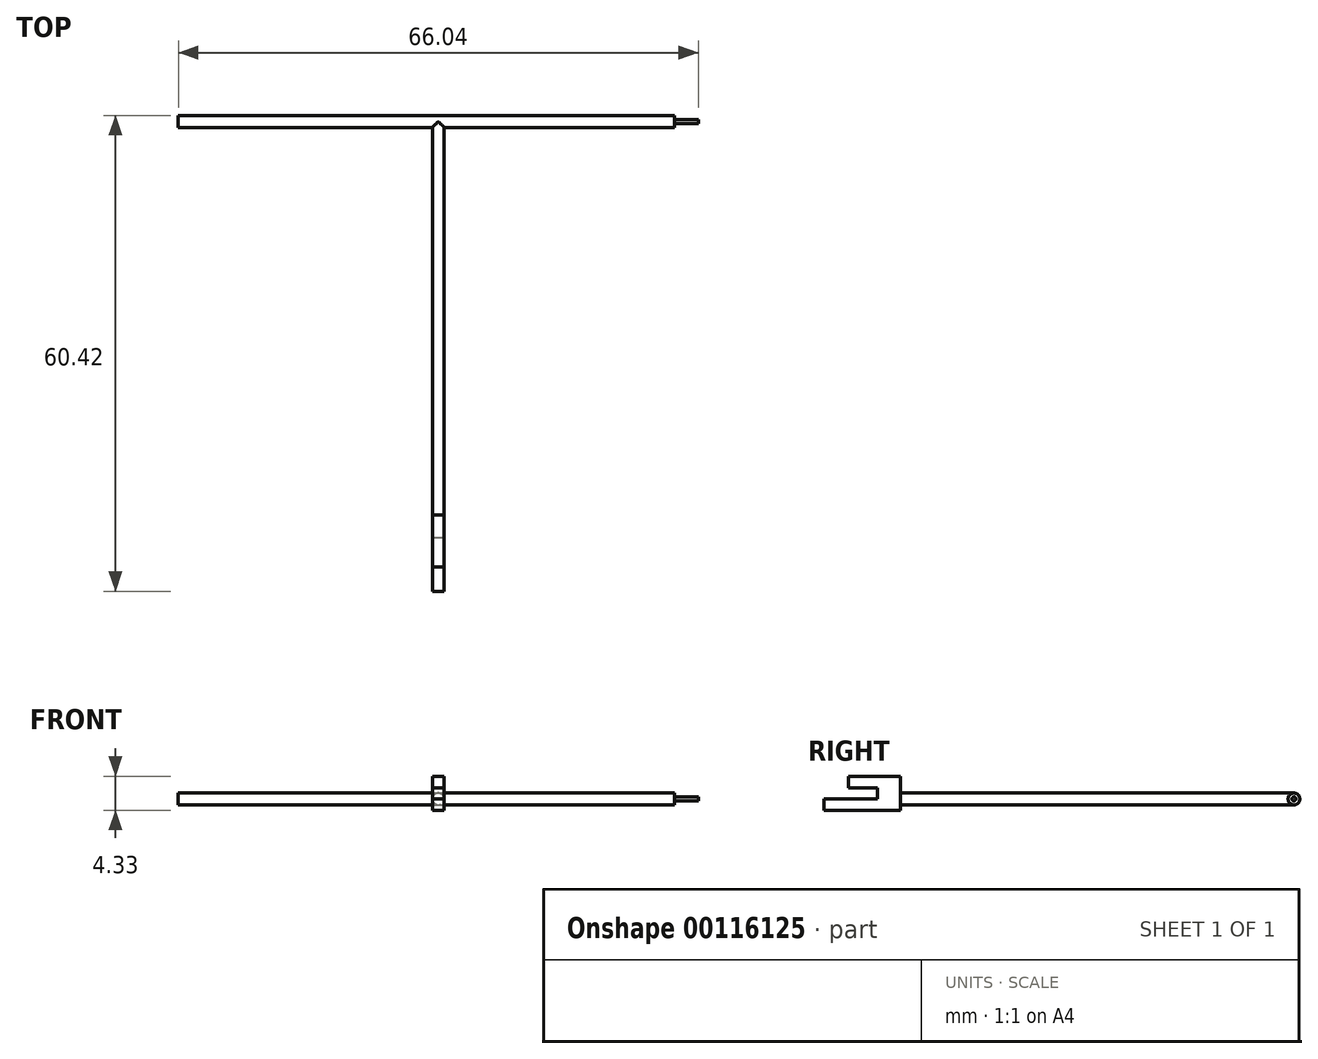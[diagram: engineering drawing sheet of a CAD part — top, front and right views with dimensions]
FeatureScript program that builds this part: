
annotation { "Feature Type Name" : "Feature", "Feature Type Description" : "" }
export const myFeature = defineFeature(function(context is Context, id is Id, definition is map)
    precondition{}
    {
        {
            var Q0;
            Q0=qCreatedBy(makeId("Front.planeOp"),FACE);
            var sketch = newSketch(context, id + "F0", { "sketchPlane" : qUnion([Q0])});
            skLineSegment(sketch, "E0", {"start": v(0, 0) * mm, "end": v(-30, 0) * mm});
            skLineSegment(sketch, "E1", {"start": v(0, 0) * mm, "end": v(30, 0) * mm});
            skLineSegment(sketch, "E2", {"start": v(30, 0) * mm, "end": v(35, 0) * mm});
            skLineSegment(sketch, "E3", {"start": v(-30, 0) * mm, "end": v(-35, 0) * mm});
            skSolve(sketch);
        }
        {
            var Q0;
            Q0=sQuery(id+"F0.wireOp",VERTEX,"E3.start");
            var Q1;
            Q1=qCreatedBy(makeId("Right.planeOp"),FACE);
            cPlane(context, id + "F1", {"entities" : qUnion([Q0, Q1]), "cplaneType" : CPlaneType.PLANE_POINT, "offset" : 25.4 * mm, "width" : 152.4 * mm, "height" : 152.4 * mm});
        }
        {
            var Q0;
            Q0=qCreatedBy(id+"F1.planeOp",FACE);
            var sketch = newSketch(context, id + "F2", { "sketchPlane" : qUnion([Q0])});
            skCircle(sketch, "E4", {"center": v(0, 0) * mm, "radius": 0.75 * mm});
            skSolve(sketch);
        }
        {
            var Q0;
            Q0=makeQuery(id+"F2.imprint","IMPRINT",FACE,{"disambiguationData":[TD([[makeQuery(id+"F2.imprint","IMPRINT",EDGE,{"derivedFrom":sQuery(id+"F2.wireOp",EDGE,"E4")}),1.0]])]});
            var Q1;
            Q1=sQuery(id+"F0.wireOp",EDGE,"E0");
            var Q2;
            Q2=sQuery(id+"F0.wireOp",EDGE,"E1");
            sweep(context, id + "F3", {"profiles" : qUnion([Q0]), "path" : qUnion([Q1, Q2])});
        }
        {
            var Q0;
            Q0=qCreatedBy(makeId("Front.planeOp"),FACE);
            var sketch = newSketch(context, id + "F4", { "sketchPlane" : qUnion([Q0])});
            skLineSegment(sketch, "E5", {"start": v(0, 0) * mm, "end": v(-33.02, 0) * mm});
            skSolve(sketch);
        }
        {
            var Q0;
            Q0=sQuery(id+"F4.wireOp",VERTEX,"E5.end");
            var Q1;
            Q1=qCreatedBy(makeId("Right.planeOp"),FACE);
            cPlane(context, id + "F5", {"entities" : qUnion([Q0, Q1]), "cplaneType" : CPlaneType.PLANE_POINT, "offset" : 25.4 * mm, "width" : 152.4 * mm, "height" : 152.4 * mm});
        }
        {
            var Q0;
            Q0=qCreatedBy(id+"F5.planeOp",FACE);
            var sketch = newSketch(context, id + "F6", { "sketchPlane" : qUnion([Q0])});
            skCircle(sketch, "E6", {"center": v(0, 0) * mm, "radius": 0.25 * mm});
            skSolve(sketch);
        }
        {
            var Q0;
            Q0=makeQuery(id+"F6.imprint","IMPRINT",FACE,{"disambiguationData":[TD([[makeQuery(id+"F6.imprint","IMPRINT",EDGE,{"derivedFrom":sQuery(id+"F6.wireOp",EDGE,"E6")}),1.0]])]});
            var Q1;
            Q1 = qSketchRegion(id + "F2", true);
            var Q2;
            Q2=sQuery(id+"F4.wireOp",EDGE,"E5");
            sweep(context, id + "F7", {"operationType" : NewBodyOperationType.ADD, "profiles" : qUnion([Q0, Q1]), "path" : qUnion([Q2])});
        }
        {
            var Q0;
            Q0=qCreatedBy(makeId("Front.planeOp"),FACE);
            var sketch = newSketch(context, id + "F8", { "sketchPlane" : qUnion([Q0])});
            skLineSegment(sketch, "E7", {"start": v(0, 0) * mm, "end": v(33.02, 0) * mm});
            skSolve(sketch);
        }
        {
            var Q0;
            Q0=sQuery(id+"F8.wireOp",VERTEX,"E7.end");
            var Q1;
            Q1=qCreatedBy(makeId("Right.planeOp"),FACE);
            cPlane(context, id + "F9", {"entities" : qUnion([Q0, Q1]), "cplaneType" : CPlaneType.PLANE_POINT, "offset" : 25.4 * mm, "width" : 152.4 * mm, "height" : 152.4 * mm});
        }
        {
            var Q0;
            Q0=qCreatedBy(id+"F9.planeOp",FACE);
            var sketch = newSketch(context, id + "F10", { "sketchPlane" : qUnion([Q0])});
            skCircle(sketch, "E8", {"center": v(0, 0) * mm, "radius": 0.25 * mm});
            skSolve(sketch);
        }
        {
            var Q0;
            Q0=makeQuery(id+"F10.imprint","IMPRINT",FACE,{"disambiguationData":[TD([[makeQuery(id+"F10.imprint","IMPRINT",EDGE,{"derivedFrom":sQuery(id+"F10.wireOp",EDGE,"E8")}),1.0]])]});
            var Q1;
            Q1=sQuery(id+"F8.wireOp",EDGE,"E7");
            sweep(context, id + "F11", {"operationType" : NewBodyOperationType.ADD, "profiles" : qUnion([Q0]), "path" : qUnion([Q1])});
        }
        {
            var Q0;
            Q0=qCreatedBy(makeId("Origin.pointOp"),VERTEX);
            var Q1;
            Q1=qCreatedBy(makeId("Right.planeOp"),FACE);
            cPlane(context, id + "F12", {"entities" : qUnion([Q0, Q1]), "cplaneType" : CPlaneType.PLANE_POINT, "offset" : 25.4 * mm, "width" : 152.4 * mm, "height" : 152.4 * mm});
        }
        {
            var Q0;
            Q0=qCreatedBy(id+"F12.planeOp",FACE);
            var sketch = newSketch(context, id + "F13", { "sketchPlane" : qUnion([Q0])});
            skLineSegment(sketch, "E9", {"start": v(0, 0) * mm, "end": v(-50, 0) * mm});
            skSolve(sketch);
        }
        {
            var Q0;
            Q0=sQuery(id+"F13.wireOp",VERTEX,"E9.end");
            var Q1;
            Q1=qCreatedBy(makeId("Front.planeOp"),FACE);
            cPlane(context, id + "F14", {"entities" : qUnion([Q0, Q1]), "cplaneType" : CPlaneType.PLANE_POINT, "offset" : 25.4 * mm, "width" : 152.4 * mm, "height" : 152.4 * mm});
        }
        {
            var Q0;
            Q0=qCreatedBy(id+"F14.planeOp",FACE);
            var sketch = newSketch(context, id + "F15", { "sketchPlane" : qUnion([Q0])});
            skCircle(sketch, "E10", {"center": v(0, 0) * mm, "radius": 0.75 * mm});
            skSolve(sketch);
        }
        {
            var Q0;
            Q0=makeQuery(id+"F15.imprint","IMPRINT",FACE,{"disambiguationData":[TD([[makeQuery(id+"F15.imprint","IMPRINT",EDGE,{"derivedFrom":sQuery(id+"F15.wireOp",EDGE,"E10")}),1.0]])]});
            var Q1;
            Q1=sQuery(id+"F13.wireOp",EDGE,"E9");
            sweep(context, id + "F16", {"operationType" : NewBodyOperationType.ADD, "profiles" : qUnion([Q0]), "path" : qUnion([Q1])});
        }
        {
            var Q0;
            Q0=sQuery(id+"F13.wireOp",VERTEX,"E9.end");
            var Q1;
            Q1=qCreatedBy(makeId("Right.planeOp"),FACE);
            cPlane(context, id + "F17", {"entities" : qUnion([Q0, Q1]), "cplaneType" : CPlaneType.PLANE_POINT, "offset" : 25.4 * mm, "width" : 152.4 * mm, "height" : 152.4 * mm});
        }
        {
            var Q0;
            Q0=qCreatedBy(id+"F17.planeOp",FACE);
            var sketch = newSketch(context, id + "F18", { "sketchPlane" : qUnion([Q0])});
            skLineSegment(sketch, "E11", {"start": v(-50, 0) * mm, "end": v(-50, 2.89) * mm});
            skLineSegment(sketch, "E12", {"start": v(-50, 2.89) * mm, "end": v(-56.6, 2.89) * mm});
            skLineSegment(sketch, "E13", {"start": v(-56.6, 2.89) * mm, "end": v(-56.6, 1.39) * mm});
            skLineSegment(sketch, "E14", {"start": v(-56.6, 1.39) * mm, "end": v(-52.88, 1.39) * mm});
            skLineSegment(sketch, "E15", {"start": v(-52.88, 1.39) * mm, "end": v(-52.88, 0) * mm});
            skLineSegment(sketch, "E16", {"start": v(-52.88, 0) * mm, "end": v(-59.67, 0) * mm});
            skLineSegment(sketch, "E17", {"start": v(-59.67, 0) * mm, "end": v(-59.67, -1.44) * mm});
            skLineSegment(sketch, "E18", {"start": v(-59.67, -1.44) * mm, "end": v(-50, -1.44) * mm});
            skLineSegment(sketch, "E19", {"start": v(-50, -1.44) * mm, "end": v(-50, 0) * mm});
            skSolve(sketch);
        }
        {
            var Q0;
            Q0=makeQuery(id+"F18.imprint","IMPRINT",FACE,{"disambiguationData":[TD([[makeQuery(id+"F18.imprint","IMPRINT",EDGE,{"derivedFrom":sQuery(id+"F18.wireOp",EDGE,"E11")}),1.0]])]});
            extrude(context, id + "F19", {"entities" : qUnion([Q0]), "operationType" : NewBodyOperationType.ADD, "endBound" : BoundingType.SYMMETRIC, "depth" : 1.5 * mm});
        }
    });
